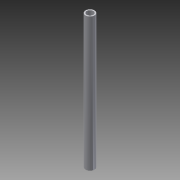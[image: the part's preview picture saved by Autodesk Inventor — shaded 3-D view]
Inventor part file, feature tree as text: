
AUTODESK INVENTOR PART (.ipt)
format: ipt  version: 2015 (Build 190159000, 159)  size: 89,088 bytes
history: native  units: mm
features: extrude x2, sketch x2, other x1
ambient origin geometry x8: Origin, YZ Plane, XZ Plane, XY Plane, X Axis, Y Axis, Z Axis, Center Point
bodies: Body1 (feature_tree)
feature tree (5):
  other  "ソリッド1"
  extrude  "押し出し1"  Depth=4.0mm
  extrude  "押し出し2"  Depth=60.0mm TaperAngle=0.0deg
  sketch  "スケッチ1"
  sketch  "スケッチ2"
